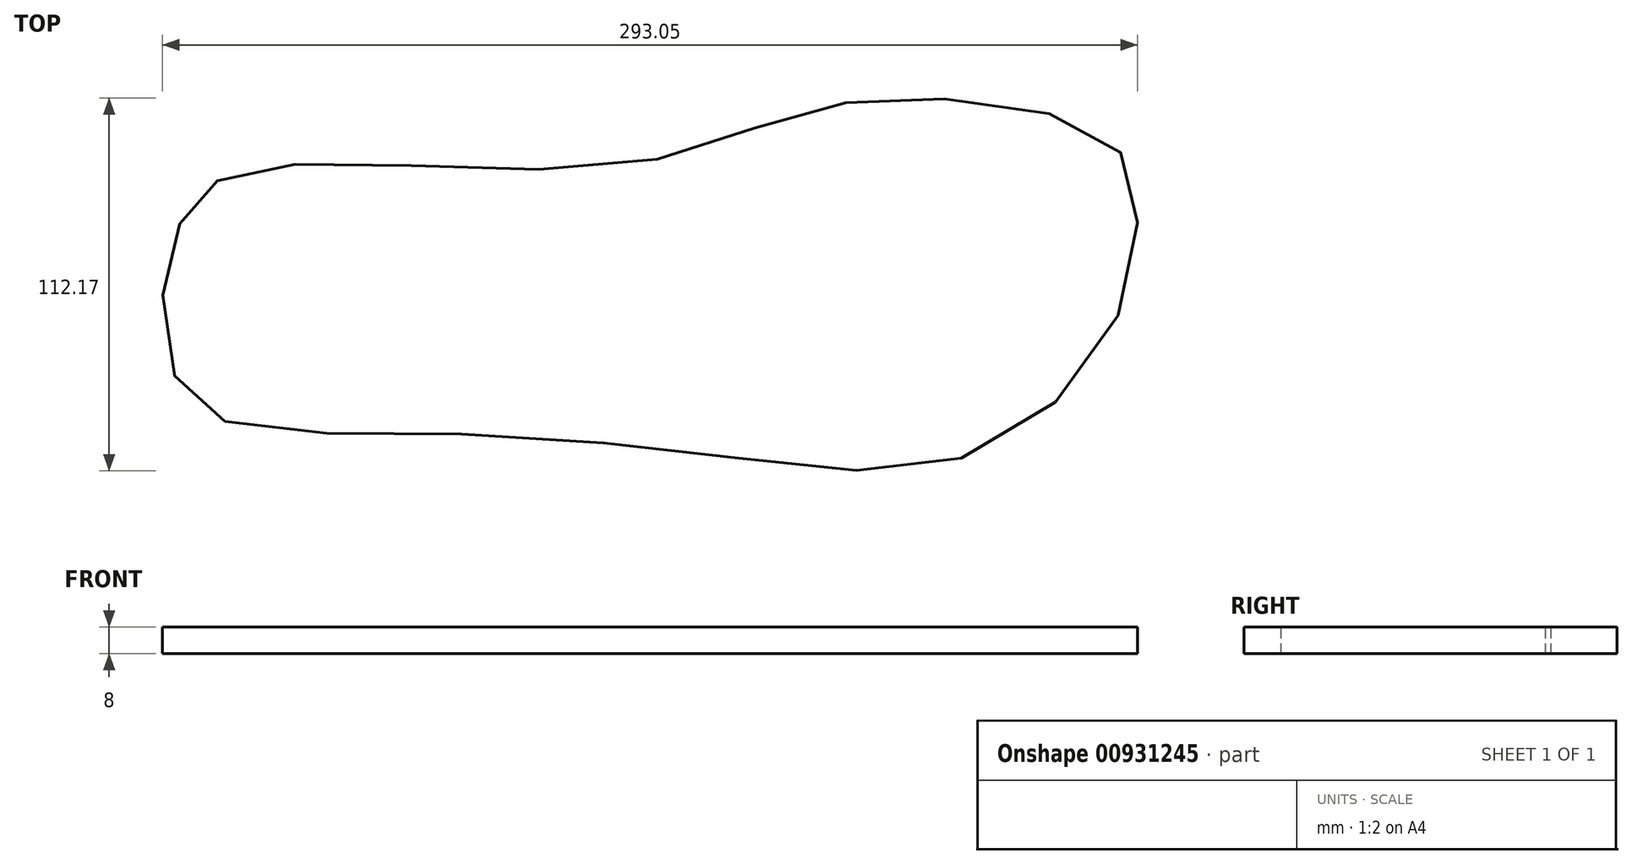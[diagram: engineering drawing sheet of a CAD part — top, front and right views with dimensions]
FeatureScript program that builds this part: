
annotation { "Feature Type Name" : "Feature", "Feature Type Description" : "" }
export const myFeature = defineFeature(function(context is Context, id is Id, definition is map)
    precondition{}
    {
        {
            var Q0;
            Q0=qCreatedBy(makeId("Top.planeOp"),FACE);
            var sketch = newSketch(context, id + "F0", { "sketchPlane" : qUnion([Q0])});
            skFitSpline(sketch, "E0", {"points": [v(-59.5, 35.34) * mm, v(-111.95, 33.28) * mm, v(-125.33, 23.95) * mm, v(-133.4, 4.5) * mm, v(-130.83, -27.38) * mm, v(-114, -42.01) * mm, v(-45.16, -45.35) * mm, v(46.36, -53.52) * mm, v(104.69, -52.97) * mm, v(148.62, -18.38) * mm, v(158.62, 23.15) * mm, v(149.31, 43.71) * mm, v(105.2, 55.15) * mm, v(59.43, 51.88) * mm, v(13.67, 37.18) * mm, v(-59.5, 35.34) * mm]});
            skSolve(sketch);
        }
        {
            var Q0;
            Q0=makeQuery(id+"F0.imprint","IMPRINT",FACE,{"disambiguationData":[TD([[makeQuery(id+"F0.imprint","IMPRINT",EDGE,{"derivedFrom":sQuery(id+"F0.wireOp",EDGE,"E0")}),1.0]])]});
            extrude(context, id + "F1", {"entities" : qUnion([Q0]), "oppositeDirection" : true, "depth" : 8 * mm, "offsetDistance" : 25 * mm});
        }
    });
